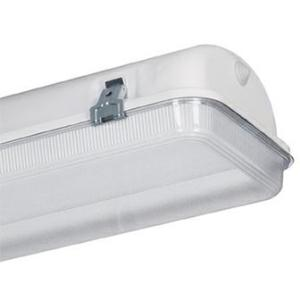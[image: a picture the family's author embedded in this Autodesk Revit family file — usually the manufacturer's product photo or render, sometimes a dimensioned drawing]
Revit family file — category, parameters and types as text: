
# Revit family: 3f_filippi_-_beta_i3f_75_pc_concentrato_3f_filippi_-_55006_-_i3f_led_752x30w_conc_l1565
name_source: partatom
category: Lighting Fixtures
units: mm (PartAtom-declared; Revit-internal decimal feet)

## family parameters
Cut with Voids When Loaded = No
Host = Face
Light Source = No
Part Type = Normal
Room Calculation Point = No
Round Connector Dimension = Use Diameter
Shared = No

## types (1)
- 3F Filippi - Beta i3F 75 PC Concentrato (1 x LED, 9597 lm, 66 W, 4000 K)
    Apparent Load = 66 VA
    Approval mark = ENEC
    CIE Flux Codes = 58 86 97 97 100
    Color Rendering = 80
    Color Temperature = 4000 K
    Control Gear = Electronic ballast
    Default Elevation = 1800 mm
    Description = ILLUMINOTECHNICAL
Luminous efficiency 100% (DLOR 97%, ULOR 3%).
Initial luminous flux of the luminaire 9597 lm.
Concentrated elliptical distribution.
Installation Interdistance Transv.D = 0.89 x hu - Long.D = 1.19 x hu.
Tabular UGR (CIE 117 - 4H-8H; S=0.25H; 70/50/20): RUG 18 - 22.4.
Beam angle: 65° - 99°.
Luminous efficacy 145 lm/W.
Lifetime (L93/B10): 30000 h. (tq+25°C)
Lifetime (L90/B10): 50000 h. (tq+25°C)
Lifetime (L85/B10): 80000 h. (tq+25°C)
Lifetime (L80/B10): 100000 h. (tq+25°C)
Lifetime (L85/B10): 50000 h. (tq+35°C)
Sudden decreased luminous flux after 50000 hours: 0% (C0).
Photobiological safety in compliance with IEC/TR 62778: RG0 risk exempt, (IEC 62471).
In compliance with IEC/EN 62722-2-1 - IEC/EN 62717 standards.

SOURCE
2 linear LED modules 30W/840.
Energy efficiency class (UE 2019/2020 - UE 2019/2015): D.
CIE 13.3 Colour rendering index: CRI >80 (R9 <50%).
IES TM-30 Fidelity Index: Rf = 84 Rg = 95.
CCT nominal colour temperature 4000 K.
Colour initial tolerance (MacAdam): SDCM 3.

MECHANICAL
Single-piece housing in pressed steel, powder-coated in white epoxy-polyester.
Diffuser in self-extinguishing V2 polycarbonate, photo-engraved interior, UV stabilised, injection moulded, with smooth outer surface, sealing gasket, hinged opening by means of galvanised steel clips.
Concentrated flow recuperator, oversized, in specular aluminium with superficial titanium-magnesium treatment, non-iridescent.
Gear-tray unit in hot-galvanised steel, painted in white polyester, fixed to the housing by means of "Ribloc" rapid devices in galvanised steel, hinged opening.
Luminaire with limited surface temperature. - D - (EN 60598-2-24)
Dimensions: 1565x235 mm, height 135 mm. Weight 6.985 kg.
IP65 protection degree.
Mechanical strength to impacts IK10 (20 joule).
Glow-wire test resistance 850°C.

ELECTRICAL
Halogen Free electronic wiring 230V-50/60Hz, power factor 0.97, THD <25%, constant output current, SELV, class I, 1 driver.
Power of the luminaire 66 W.
CE - IEC 60598-1 - EN 60598-1.
SAFE FLICKER: PstLM=<1 and SVM=<0.4 (IEC TR 61547-1 and IEC TR 63158), to ensure a more comfortable and safe light.
Luminaire compliant with EN 60598-2-22 for power supply from a centralised emergency system CPSS (Central Power Supply System), not incorporated in the luminaire - high risk areas excluded. The default power and flux are 100% in AC and 100% in DC.
Ambient temperature from -20°C to +35°C.
Temperature class T6 max 85°C.
Relative humidity UR: <85%.

INSTALLATION
Ceiling / Suspended / Wall.
All accessories dedicated to this product are available on the Catalog and on our website www.3F-Filippi.com.

APPLICATIONS
Suitable product for food production plants (HACCP), IFS (Food Version 6), BRC (GSFS Food Version 7).
In industrial environments, stores and dry, dusty indoor environments, subject to occasional water splashes.

WARNING
Fixture not suitable for cold stores with an ambient temperature <0°C and/or relative humidity >85%.
Luminaire designed for disposal/recycling at end-of-life.
Replaceable (LED only) light source by a professional. Replaceable control gear by a professional.
    Height = 135 mm
    Lamp = 1 x LED
    Lamp Light Flux = 9597 lm
    Lamp Power = 66 W
    Lamp count = 1
    Length = 1565 mm
    Lifetime = 50000 h
    Luminous efficacy = 145 lm/W
    Manufacturer = 3F Filippi
    ModVariant = No
    Model = 3F Filippi - 55006 - i3F LED 752x30W CONC L1565
    Mounting Place = Ceiling
    Mounting Type = Pendant
    Number of Poles = 1
    OnlyDefault = Yes
    Power Factor = 1
    Product Name = 3F Filippi - Beta i3F 75 PC Concentrato
    Product group = pendant luminaire
    ProductGroupID = 9
    Protection Class = Protection class I
    Protection Degree = IP 65
    RLX_Detail_Level = 1
    RLX_Emergency_Light_Flux = 0 lm
    RLX_Emergency_Type = 0
    RLX_Emergency_Type_DB = No
    RlxData = <blob elided: 68345 chars, md5=e8262c0f>
    Socket = socket
    Standby Power = 0 W
    System Light Flux = 9597 lm
    System Power = 66 W
    Type Comments = Product without accessories
    Type Image = 3ffilippi_55006.jpg
    URL = http://relux.com
    VarID = ---
    Voltage = 0 V
    Weight = 0.00 kg
    Width = 235 mm

## geometry (parser evidence)
native form markers: Blend x4, Sweep x9
no freeform markers — native parametric forms only
